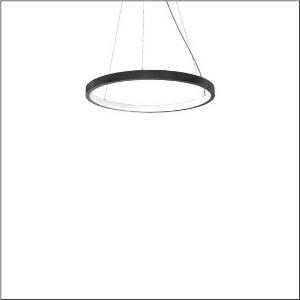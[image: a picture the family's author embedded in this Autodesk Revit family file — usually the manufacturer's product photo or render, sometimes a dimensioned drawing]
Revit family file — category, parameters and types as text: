
# Revit family: silica_21_ring-i_5pjbi2d3104a
name_source: partatom
category: Lighting Fixtures
units: mm (PartAtom-declared; Revit-internal decimal feet)

## family parameters
Cut with Voids When Loaded = No
Host = Face
Light Source = No
Part Type = Normal
Room Calculation Point = No
Round Connector Dimension = Use Diameter
Shared = No

## types (1)
- Silica 21 Ring-I (1 x LED, 5040 lm, 80 W, 4000K)
    Apparent Load = 80 VA
    CIE Flux Codes = 22 48 76 50 101
    Color Rendering = 80
    Color Temperature = 4000K
    Default Elevation = 1800 mm
    Description = Silica 21 Ring-I, suspended luminaire, of PMMA, frosted, light emission: inner ring side luminous distribution, primary light characteristic: symmetric, installation type: suspended mounting, LED, rated luminous flux: 5.040lm, luminous efficacy: 63lm/W, light colour: 840, colour temperature: 4000K, control gear: DALI 2, with terminal, 5-pole, mains connection: 230V, AC/DC, 0/50..60Hz, rated input power: 80W, housing, of extruded aluminium section, jet black (RAL 9005), diameter: 805mm, ceiling canopy, jet black (RAL 9005), protection rating (lamp compartment): IP40, insulation class (complete): insulation class I (protective earthing), certification: CE, impact resistance: IK02, permissible operating ambient temperature: 0..+35°C, packaging unit: 1 piece
    Height = 48 mm  [stored 0.15748 ft]
    Lamp = 1 x LED
    Lamp Light Flux = 5040 lm
    Lamp Power = 80 W
    Lamp count = 1
    Length = 805 mm
    Luminous efficacy = 63 lm/W
    Manufacturer = Siteco
    ModVariant = No
    Model = 5PJBI2D3104A
    Mounting Place = Ceiling
    Mounting Type = Pendant
    Number of Poles = 1
    OnlyDefault = Yes
    Power Factor = 1
    Product Name = Silica 21 Ring-I
    Product group = suspended luminaire
    ProductGroupID = 904
    Protection Class = Protection class I
    Protection Degree = IP 40
    RLX_Detail_Level = 1
    RLX_Emergency_Light_Flux = 0 lm
    RLX_Emergency_Type = 0
    RLX_Emergency_Type_DB = No
    RlxData = <blob elided: 13921 chars, md5=36d7e0da>
    Socket = socket
    Standby Power = 0 W
    System Light Flux = 5040 lm
    System Power = 80 W
    Type Comments = Product without accessories
    Type Image = l_1258365.jpg
    URL = http://relux.com
    VarID = ---
    Voltage = 0 V
    Weight = 0.00 kg
    Width = 0 mm  [stored 0 ft]

note: [stored X ft] marks values corroborated as IEEE doubles in the binary element streams (Revit-internal decimal feet)

## geometry (parser evidence)
native form markers: Sweep x13
no freeform markers — native parametric forms only
